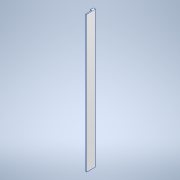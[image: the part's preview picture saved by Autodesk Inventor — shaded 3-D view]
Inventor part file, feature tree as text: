
AUTODESK INVENTOR PART (.ipt)
format: ipt  version: 2022 (Build 260153000, 153)  size: 100,352 bytes
history: native  units: mm
features: sketch x2, extrude x1
ambient origin geometry x8: Origin, YZ Plane, XZ Plane, XY Plane, X Axis, Y Axis, Z Axis, Center Point
bodies: Solid1 (feature_tree)
feature tree (3):
  sketch  "Sketch1"  dims[d0=44.0mm d1=6.0mm]
  extrude  "Extrusion1"  Depth=6.0mm
  sketch  "Sketch2"  dims[d2=10.0mm d3=65.0mm d4=1000.0mm d5=0.0mm]
